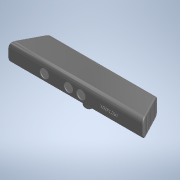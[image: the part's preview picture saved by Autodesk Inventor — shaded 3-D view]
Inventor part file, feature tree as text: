
AUTODESK INVENTOR PART (.ipt)
format: ipt  version: 2020 (Build 240168000, 168)  size: 468,480 bytes
history: mixed  units: mm (DEFAULTED — no unit token found)
features: fillet x1, imported_body x1
ambient origin geometry x8: Origin, YZ Plane, XZ Plane, XY Plane, X Axis, Y Axis, Z Axis, Center Point
bodies: Solid1 (imported_parasolid)
feature tree (2):
  fillet  "Fillet3"  [1 undecoded]
  imported_body  NMx_Import_Brep_tag  [imported B-rep: ~6 faces, bbox_mm=None]
note: 1 required parameter value undecoded (feature->parameter linkage not recoverable at this tier; creation-order binding heuristic only, values carry confidence <= 0.55)
